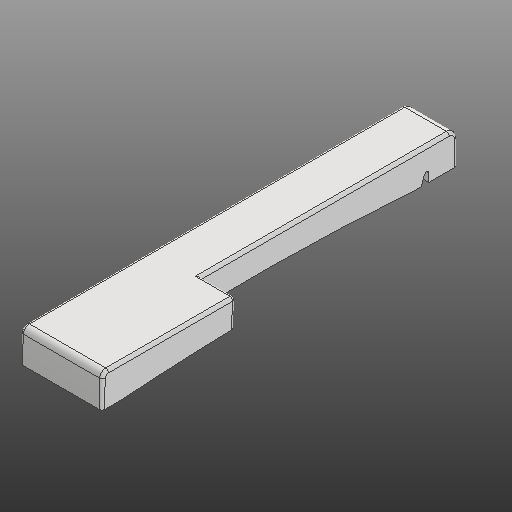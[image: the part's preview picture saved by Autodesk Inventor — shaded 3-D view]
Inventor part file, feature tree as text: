
AUTODESK INVENTOR PART (.ipt)
format: ipt  version: 2020 (Build 240168000, 168)  size: 321,024 bytes
history: native  units: in
note: dims shown in document units (in); Inventor stores cm internally (conversion verified against a paired STEP export)
features: extrude x4, other x3, fillet x2
ambient origin geometry x8: Origin, YZ Plane, XZ Plane, XY Plane, X Axis, Y Axis, Z Axis, Center Point
bodies: Solid1 (feature_tree)
feature tree (9):
  other  "Slot Start Plane"
  other  "Key Profile"
  extrude  "Upper (u)"  TaperAngle=0.0deg  [1 undecoded]
  extrude  "Lower (d)"  TaperAngle=0.0deg  [1 undecoded]
  extrude  "Protrusion Cutout"  Depth=0.0591in
  fillet  "Front Fillet"  Radius=0.1374in
  extrude  "Slot"  [1 undecoded]
  fillet  "Edge Softening"  Radius=0.0787in
  other  "Slot Sketch"
note: 3 required parameter values undecoded (feature->parameter linkage not recoverable at this tier; creation-order binding heuristic only, values carry confidence <= 0.55)
